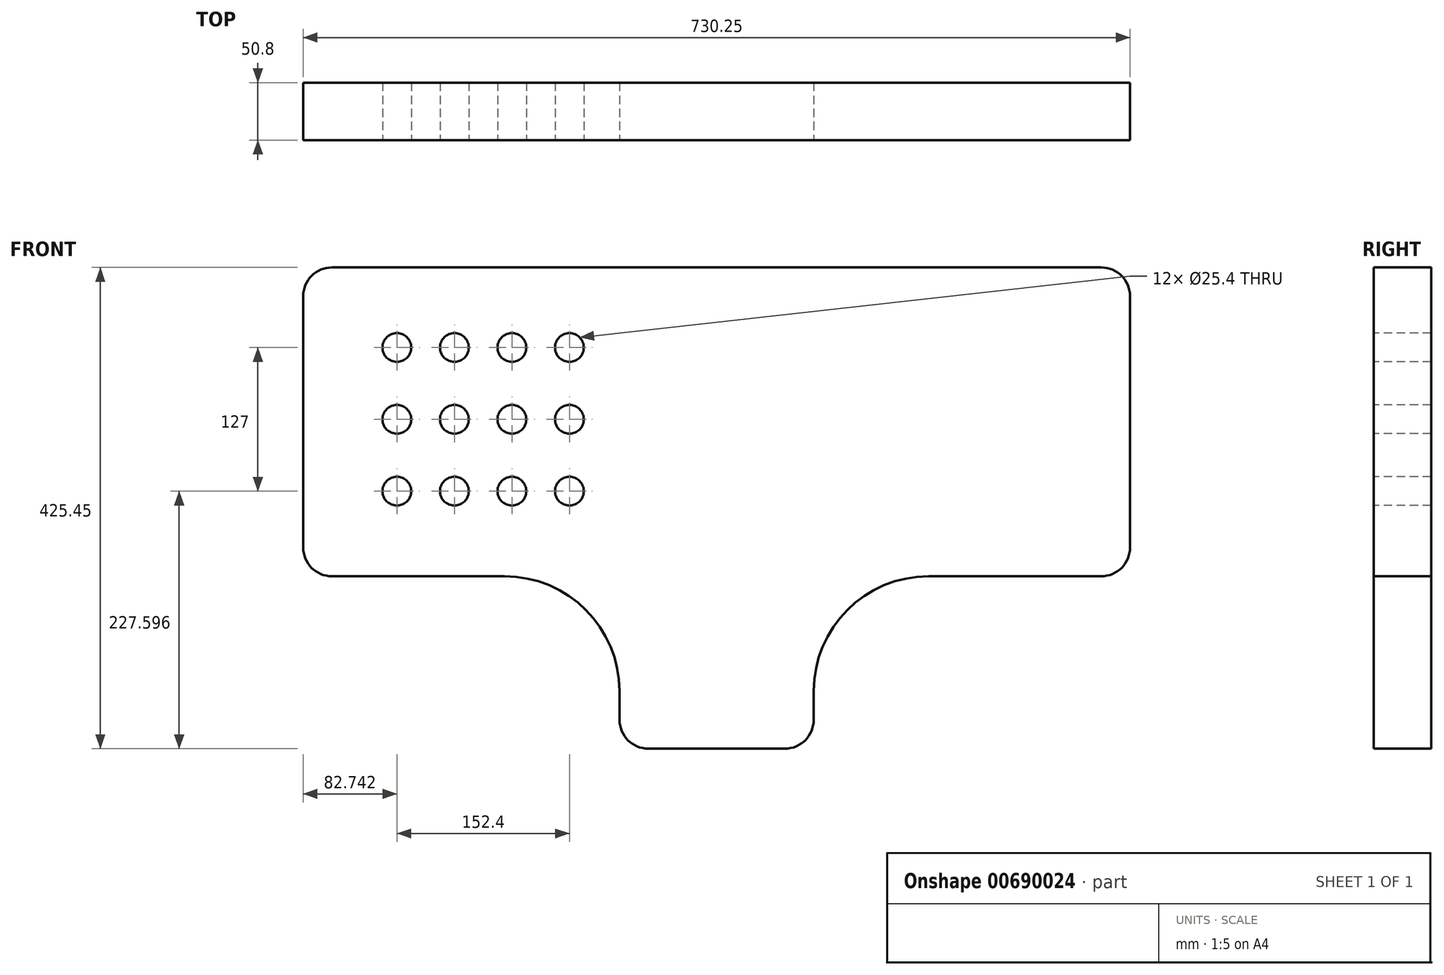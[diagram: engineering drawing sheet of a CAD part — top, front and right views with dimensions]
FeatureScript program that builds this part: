
annotation { "Feature Type Name" : "Feature", "Feature Type Description" : "" }
export const myFeature = defineFeature(function(context is Context, id is Id, definition is map)
    precondition{}
    {
        {
            var Q0;
            Q0=qCreatedBy(makeId("Front.planeOp"),FACE);
            var sketch = newSketch(context, id + "F0", { "sketchPlane" : qUnion([Q0])});
            skLineSegment(sketch, "E0.bottom", {"start": v(285.75, 0) * mm, "end": v(406.4, 0) * mm});
            skLineSegment(sketch, "E0.top", {"start": v(6.35, 425.45) * mm, "end": v(685.8, 425.45) * mm});
            skLineSegment(sketch, "E0.left", {"start": v(-19.05, 177.8) * mm, "end": v(-19.05, 400.05) * mm});
            skLineSegment(sketch, "E0.right", {"start": v(711.2, 177.8) * mm, "end": v(711.2, 400.05) * mm});
            skLineSegment(sketch, "E1", {"start": v(6.35, 152.4) * mm, "end": v(158.75, 152.4) * mm});
            skLineSegment(sketch, "E2", {"start": v(260.35, 50.8) * mm, "end": v(260.35, 25.4) * mm});
            skPoint(sketch, "E3.visualSharp", {"position": v(-19.05, 152.4) * mm});
            skArc(sketch, "E3.filletArc", {"start": v(-19.05, 177.8) * mm, "mid": v(-11.61, 159.84) * mm, "end": v(6.35, 152.4) * mm});
            skPoint(sketch, "E4.visualSharp", {"position": v(260.35, 152.4) * mm});
            skArc(sketch, "E4.filletArc", {"start": v(260.35, 50.8) * mm, "mid": v(230.6, 122.64) * mm, "end": v(158.75, 152.4) * mm});
            skPoint(sketch, "E5.visualSharp", {"position": v(-19.05, 425.45) * mm});
            skArc(sketch, "E5.filletArc", {"start": v(6.35, 425.45) * mm, "mid": v(-11.61, 418.01) * mm, "end": v(-19.05, 400.05) * mm});
            skPoint(sketch, "E6.visualSharp", {"position": v(711.2, 425.45) * mm});
            skArc(sketch, "E6.filletArc", {"start": v(711.2, 400.05) * mm, "mid": v(703.76, 418.01) * mm, "end": v(685.8, 425.45) * mm});
            skLineSegment(sketch, "E7", {"start": v(431.8, 25.4) * mm, "end": v(431.8, 50.8) * mm});
            skLineSegment(sketch, "E8", {"start": v(533.4, 152.4) * mm, "end": v(685.8, 152.4) * mm});
            skPoint(sketch, "E9.visualSharp", {"position": v(431.8, 152.4) * mm});
            skArc(sketch, "E9.filletArc", {"start": v(533.4, 152.4) * mm, "mid": v(461.56, 122.64) * mm, "end": v(431.8, 50.8) * mm});
            skPoint(sketch, "E10.visualSharp", {"position": v(711.2, 152.4) * mm});
            skArc(sketch, "E10.filletArc", {"start": v(685.8, 152.4) * mm, "mid": v(703.76, 159.84) * mm, "end": v(711.2, 177.8) * mm});
            skPoint(sketch, "E11.visualSharp", {"position": v(431.8, 0) * mm});
            skArc(sketch, "E11.filletArc", {"start": v(406.4, 0) * mm, "mid": v(424.36, 7.44) * mm, "end": v(431.8, 25.4) * mm});
            skPoint(sketch, "E12.visualSharp", {"position": v(260.35, 0) * mm});
            skArc(sketch, "E12.filletArc", {"start": v(260.35, 25.4) * mm, "mid": v(267.79, 7.44) * mm, "end": v(285.75, 0) * mm});
            skCircle(sketch, "E13", {"center": v(63.7, 354.6) * mm, "radius": 12.7 * mm});
            skCircle(sketch, "E14.0.1.0", {"center": v(63.7, 291.1) * mm, "radius": 12.7 * mm});
            skCircle(sketch, "E14.0.2.0", {"center": v(63.7, 227.6) * mm, "radius": 12.7 * mm});
            skCircle(sketch, "E14.1.0.0", {"center": v(114.5, 354.6) * mm, "radius": 12.7 * mm});
            skCircle(sketch, "E14.1.1.0", {"center": v(114.5, 291.1) * mm, "radius": 12.7 * mm});
            skCircle(sketch, "E14.1.2.0", {"center": v(114.5, 227.6) * mm, "radius": 12.7 * mm});
            skCircle(sketch, "E14.2.0.0", {"center": v(165.3, 354.6) * mm, "radius": 12.7 * mm});
            skCircle(sketch, "E14.2.1.0", {"center": v(165.3, 291.1) * mm, "radius": 12.7 * mm});
            skCircle(sketch, "E14.2.2.0", {"center": v(165.3, 227.6) * mm, "radius": 12.7 * mm});
            skCircle(sketch, "E14.3.0.0", {"center": v(216.1, 354.6) * mm, "radius": 12.7 * mm});
            skCircle(sketch, "E14.3.1.0", {"center": v(216.1, 291.1) * mm, "radius": 12.7 * mm});
            skCircle(sketch, "E14.3.2.0", {"center": v(216.1, 227.6) * mm, "radius": 12.7 * mm});
            skLineSegment(sketch, "E14.direction1", {"start": v(63.7, 354.6) * mm, "end": v(114.5, 354.6) * mm, "construction": true});
            skLineSegment(sketch, "E14.direction2", {"start": v(63.7, 354.6) * mm, "end": v(63.7, 291.1) * mm, "construction": true});
            skSolve(sketch);
        }
        {
            var Q0;
            Q0=makeQuery(id+"F0.imprint","IMPRINT",FACE,{"disambiguationData":[TD([[makeQuery(id+"F0.imprint","IMPRINT",EDGE,{"derivedFrom":sQuery(id+"F0.wireOp",EDGE,"E0.bottom")}),1.0]])]});
            extrude(context, id + "F1", {"entities" : qUnion([Q0]), "oppositeDirection" : true, "depth" : 50.8 * mm, "offsetDistance" : 25.4 * mm});
        }
    });
